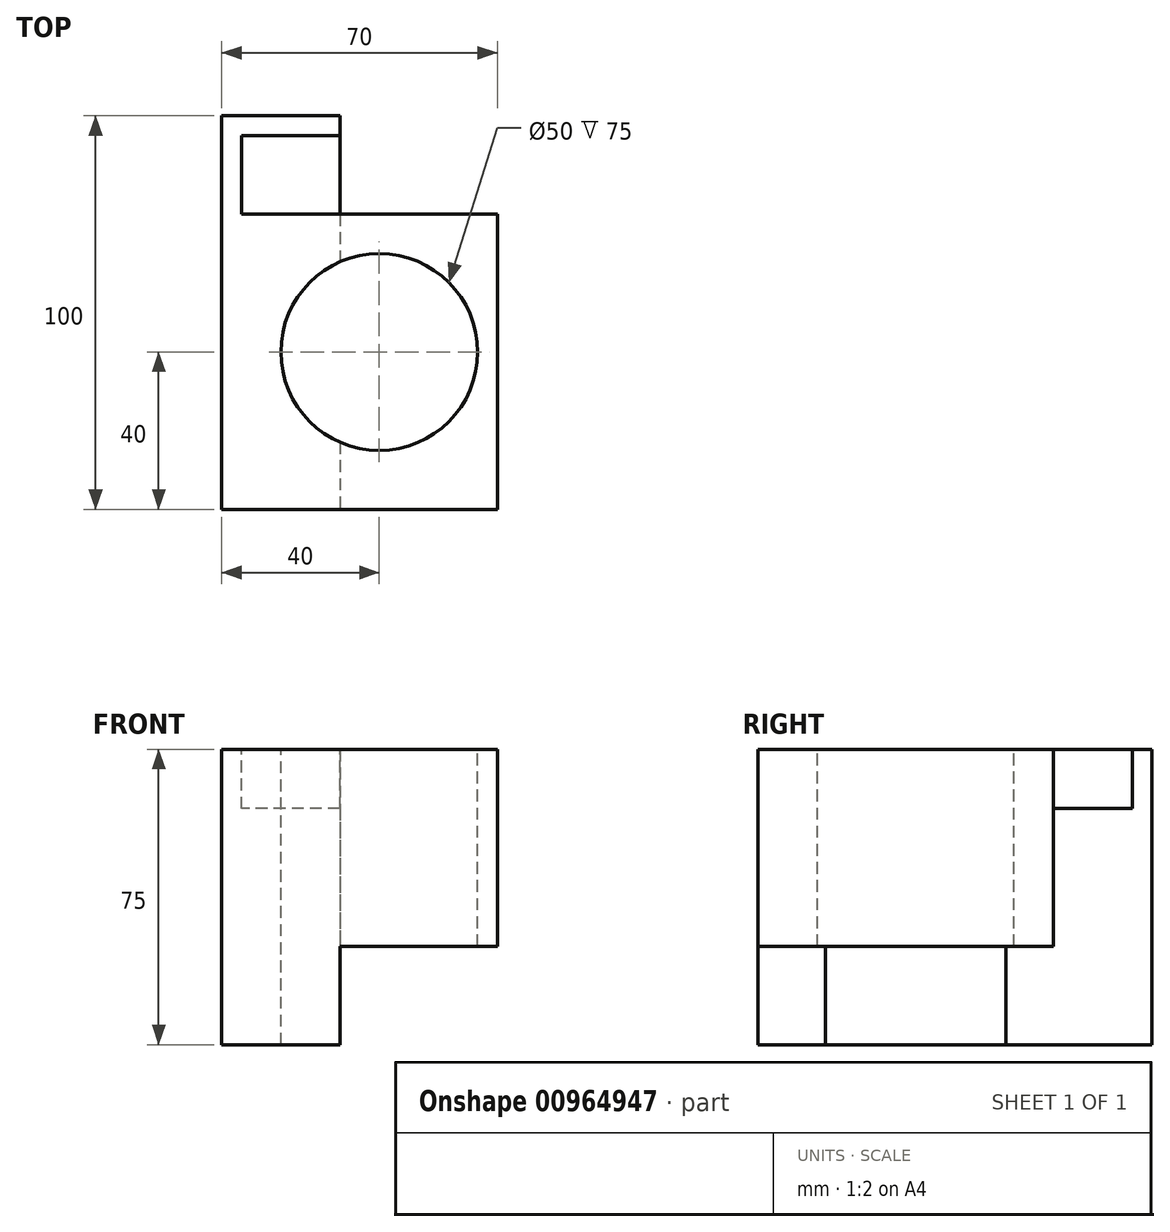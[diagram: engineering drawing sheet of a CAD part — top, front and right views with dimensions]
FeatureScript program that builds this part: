
annotation { "Feature Type Name" : "Feature", "Feature Type Description" : "" }
export const myFeature = defineFeature(function(context is Context, id is Id, definition is map)
    precondition{}
    {
        {
            var Q0;
            Q0=qCreatedBy(makeId("Top.planeOp"),FACE);
            var sketch = newSketch(context, id + "F0", { "sketchPlane" : qUnion([Q0])});
            skLineSegment(sketch, "E0", {"start": v(0, 0) * mm, "end": v(0, 100) * mm});
            skLineSegment(sketch, "E1", {"start": v(0, 100) * mm, "end": v(30, 100) * mm});
            skLineSegment(sketch, "E2", {"start": v(30, 100) * mm, "end": v(30, 75) * mm});
            skLineSegment(sketch, "E3", {"start": v(30, 75) * mm, "end": v(70, 75) * mm});
            skLineSegment(sketch, "E4", {"start": v(70, 75) * mm, "end": v(70, 0) * mm});
            skLineSegment(sketch, "E5", {"start": v(70, 0) * mm, "end": v(0, 0) * mm});
            skSolve(sketch);
        }
        {
            var Q0;
            Q0 = qSketchRegion(id + "F0", true);
            extrude(context, id + "F1", {"entities" : qUnion([Q0]), "depth" : 75 * mm, "offsetDistance" : 25 * mm});
        }
        {
            var Q0;
            Q0=makeQuery(id+"F1.opExtrude","SWEPT_FACE",FACE,{"disambiguationData":[OSD([sQuery(id+"F0.wireOp",EDGE,"E5")])]});
            var sketch = newSketch(context, id + "F2", { "sketchPlane" : qUnion([Q0])});
            skLineSegment(sketch, "E6.bottom", {"start": v(70, 0) * mm, "end": v(30, 0) * mm});
            skLineSegment(sketch, "E6.top", {"start": v(70, 25) * mm, "end": v(30, 25) * mm});
            skLineSegment(sketch, "E6.left", {"start": v(70, 0) * mm, "end": v(70, 25) * mm});
            skLineSegment(sketch, "E6.right", {"start": v(30, 0) * mm, "end": v(30, 25) * mm});
            skSolve(sketch);
        }
        {
            var Q0;
            Q0 = qSketchRegion(id + "F2", true);
            extrude(context, id + "F3", {"entities" : qUnion([Q0]), "operationType" : NewBodyOperationType.REMOVE, "endBound" : BoundingType.THROUGH_ALL, "oppositeDirection" : true, "depth" : 25 * mm, "offsetDistance" : 25 * mm});
        }
        {
            var Q0;
            Q0=makeQuery(id+"F1.opExtrude","CAP_FACE",FACE,{"disambiguationData":[OSD([sQuery(id+"F0.wireOp",EDGE,"E0"),sQuery(id+"F0.wireOp",EDGE,"E1"),sQuery(id+"F0.wireOp",EDGE,"E2"),sQuery(id+"F0.wireOp",EDGE,"E3"),sQuery(id+"F0.wireOp",EDGE,"E4"),sQuery(id+"F0.wireOp",EDGE,"E5")])],"isStart":false});
            var sketch = newSketch(context, id + "F4", { "sketchPlane" : qUnion([Q0])});
            skLineSegment(sketch, "E7.bottom", {"start": v(30, 75) * mm, "end": v(5, 75) * mm});
            skLineSegment(sketch, "E7.top", {"start": v(30, 95) * mm, "end": v(5, 95) * mm});
            skLineSegment(sketch, "E7.left", {"start": v(30, 75) * mm, "end": v(30, 95) * mm});
            skLineSegment(sketch, "E7.right", {"start": v(5, 75) * mm, "end": v(5, 95) * mm});
            skSolve(sketch);
        }
        {
            var Q0;
            Q0 = qSketchRegion(id + "F4", true);
            extrude(context, id + "F5", {"entities" : qUnion([Q0]), "operationType" : NewBodyOperationType.REMOVE, "oppositeDirection" : true, "depth" : 15 * mm, "offsetDistance" : 25 * mm});
        }
        {
            var Q0;
            Q0=makeQuery(id+"F1.opExtrude","CAP_FACE",FACE,{"disambiguationData":[OSD([sQuery(id+"F0.wireOp",EDGE,"E0"),sQuery(id+"F0.wireOp",EDGE,"E1"),sQuery(id+"F0.wireOp",EDGE,"E2"),sQuery(id+"F0.wireOp",EDGE,"E3"),sQuery(id+"F0.wireOp",EDGE,"E4"),sQuery(id+"F0.wireOp",EDGE,"E5")])],"isStart":false});
            var sketch = newSketch(context, id + "F6", { "sketchPlane" : qUnion([Q0])});
            skCircle(sketch, "E8", {"center": v(40, 40) * mm, "radius": 25 * mm});
            skSolve(sketch);
        }
        {
            var Q0;
            Q0 = qSketchRegion(id + "F6", true);
            extrude(context, id + "F7", {"entities" : qUnion([Q0]), "operationType" : NewBodyOperationType.REMOVE, "endBound" : BoundingType.THROUGH_ALL, "oppositeDirection" : true, "depth" : 25 * mm, "offsetDistance" : 25 * mm});
        }
    });
